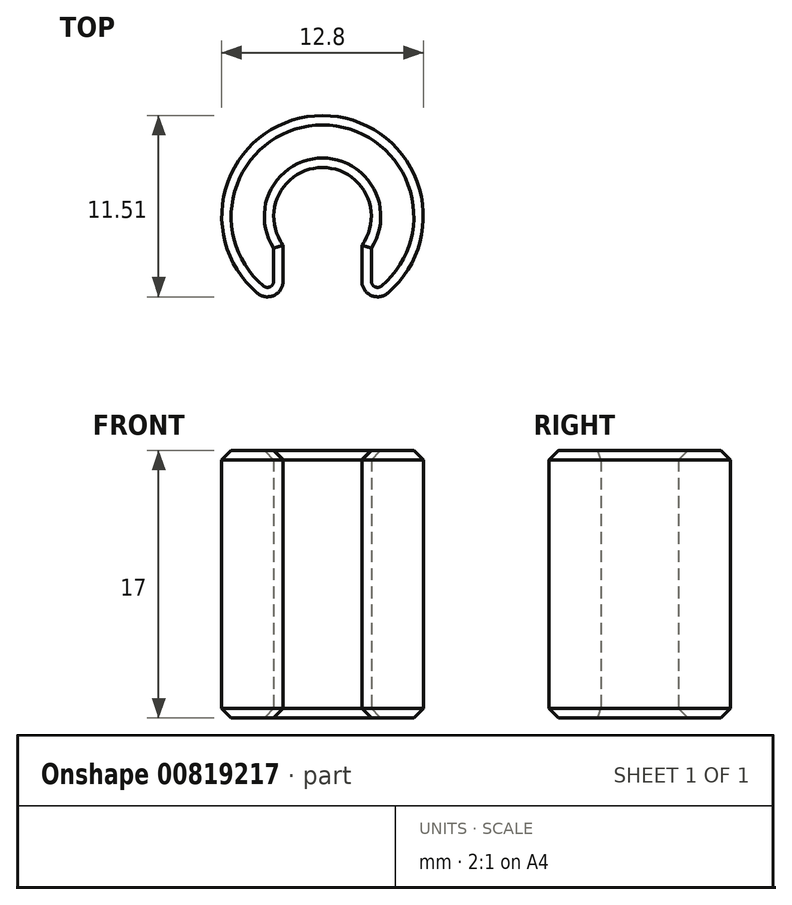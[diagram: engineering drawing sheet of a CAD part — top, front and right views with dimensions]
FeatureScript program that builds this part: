
annotation { "Feature Type Name" : "Feature", "Feature Type Description" : "" }
export const myFeature = defineFeature(function(context is Context, id is Id, definition is map)
    precondition{}
    {
        {
            var Q0;
            Q0=qCreatedBy(makeId("Top.planeOp"),FACE);
            var sketch = newSketch(context, id + "F0", { "sketchPlane" : qUnion([Q0])});
            skArc(sketch, "E0", {"start": v(2.5, -1.83) * mm, "mid": v(0, 3.1) * mm, "end": v(-2.5, -1.83) * mm});
            skArc(sketch, "E1", {"start": v(2.5, -5.9) * mm, "mid": v(0, 6.4) * mm, "end": v(-2.5, -5.9) * mm});
            skLineSegment(sketch, "E2", {"start": v(0, 0) * mm, "end": v(0, -12.21) * mm, "construction": true});
            skLineSegment(sketch, "E3", {"start": v(-2.5, -1.83) * mm, "end": v(-2.5, -5.9) * mm});
            skLineSegment(sketch, "E4", {"start": v(2.5, -1.83) * mm, "end": v(2.5, -5.9) * mm});
            skLineSegment(sketch, "E5", {"start": v(0, 0) * mm, "end": v(2.5, 0) * mm, "construction": true});
            skLineSegment(sketch, "E6", {"start": v(2.5, 0) * mm, "end": v(2.5, -10.5) * mm, "construction": true});
            skLineSegment(sketch, "E7", {"start": v(0, 0) * mm, "end": v(-2.5, 0) * mm, "construction": true});
            skLineSegment(sketch, "E8", {"start": v(-2.5, 0) * mm, "end": v(-2.5, -10.5) * mm, "construction": true});
            skSolve(sketch);
        }
        {
            var Q0;
            Q0 = qSketchRegion(id + "F0", true);
            extrude(context, id + "F1", {"entities" : qUnion([Q0]), "depth" : 17 * mm, "offsetDistance" : 25 * mm});
        }
        {
            var Q0;
            Q0=makeQuery(id+"F1.opExtrude","SWEPT_EDGE",EDGE,{"disambiguationData":[OSD([sQuery(id+"F0.wireOp",EDGE,"E1"),sQuery(id+"F0.wireOp",EDGE,"E3")])]});
            var Q1;
            Q1=makeQuery(id+"F1.opExtrude","SWEPT_EDGE",EDGE,{"disambiguationData":[OSD([sQuery(id+"F0.wireOp",EDGE,"E1"),sQuery(id+"F0.wireOp",EDGE,"E4")])]});
            fillet(context, id + "F2", {"entities" : qUnion([Q0, Q1]), "radius" : 1 * mm, "tangentPropagation" : true, "allowEdgeOverflow" : false});
        }
        {
            var Q0;
            Q0=makeQuery(id+"F1.opExtrude","CAP_FACE",FACE,{"disambiguationData":[OSD([sQuery(id+"F0.wireOp",EDGE,"E0"),sQuery(id+"F0.wireOp",EDGE,"E1"),sQuery(id+"F0.wireOp",EDGE,"E3"),sQuery(id+"F0.wireOp",EDGE,"E4")])],"isStart":false});
            var Q1;
            Q1=makeQuery(id+"F1.opExtrude","CAP_FACE",FACE,{"disambiguationData":[OSD([sQuery(id+"F0.wireOp",EDGE,"E0"),sQuery(id+"F0.wireOp",EDGE,"E1"),sQuery(id+"F0.wireOp",EDGE,"E3"),sQuery(id+"F0.wireOp",EDGE,"E4")])],"isStart":true});
            chamfer(context, id + "F3", {"entities" : qUnion([Q0, Q1]), "width" : .6 * mm, "tangentPropagation" : true});
        }
    });
